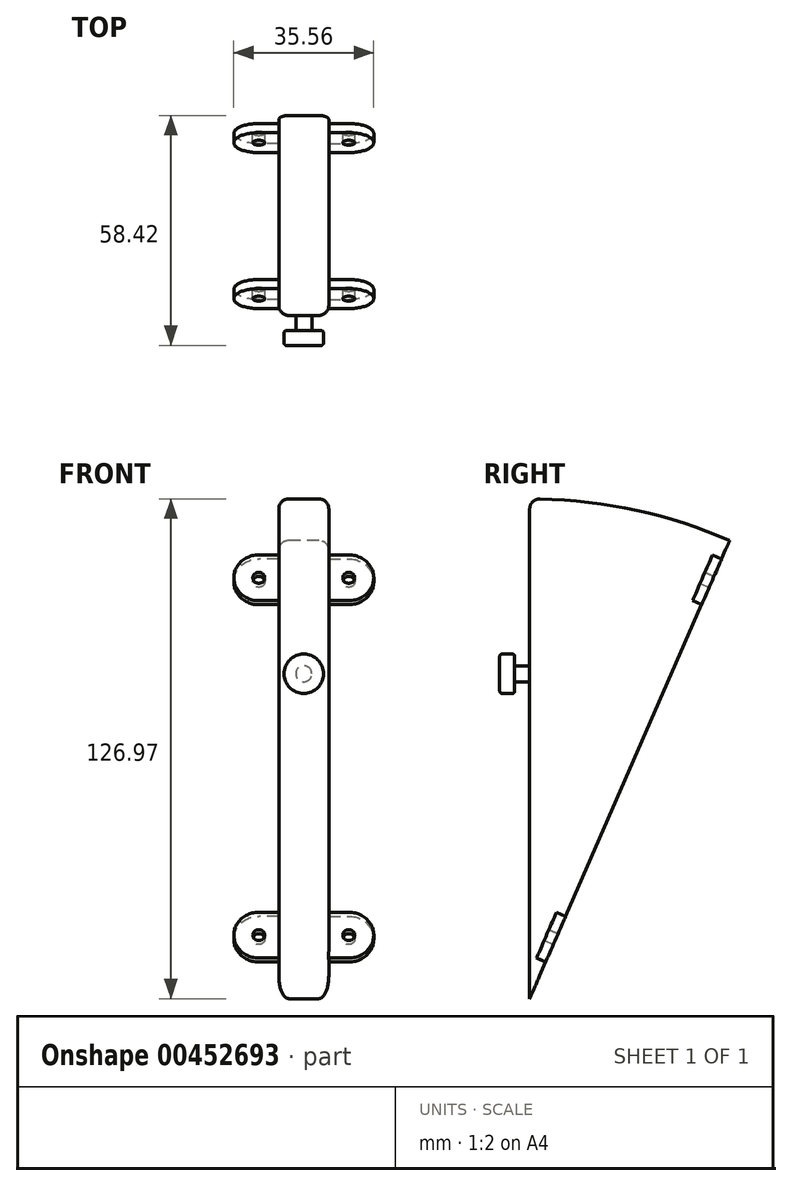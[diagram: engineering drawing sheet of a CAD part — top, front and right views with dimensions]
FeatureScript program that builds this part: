
annotation { "Feature Type Name" : "Feature", "Feature Type Description" : "" }
export const myFeature = defineFeature(function(context is Context, id is Id, definition is map)
    precondition{}
    {
        {
            var Q0;
            Q0=qCreatedBy(makeId("Front.planeOp"),FACE);
            var sketch = newSketch(context, id + "F0", { "sketchPlane" : qUnion([Q0])});
            skLineSegment(sketch, "E0", {"start": v(-25.33, 83.67) * mm, "end": v(-25.33, -43.33) * mm});
            skLineSegment(sketch, "E1", {"start": v(-25.33, -43.33) * mm, "end": v(-12.63, -43.33) * mm});
            skLineSegment(sketch, "E2", {"start": v(-12.63, -43.33) * mm, "end": v(-12.63, 83.67) * mm});
            skLineSegment(sketch, "E3", {"start": v(-12.63, 83.67) * mm, "end": v(-25.33, 83.67) * mm});
            skSolve(sketch);
        }
        {
            var Q0;
            Q0=makeQuery(id+"F0.imprint","IMPRINT",FACE,{"disambiguationData":[TD([[makeQuery(id+"F0.imprint","IMPRINT",EDGE,{"derivedFrom":sQuery(id+"F0.wireOp",EDGE,"E0")}),1.0]])]});
            var Q1;
            Q1=sQuery(id+"F0.wireOp",EDGE,"E1");
            revolve(context, id + "F1", {"entities" : qUnion([Q0]), "axis" : qUnion([Q1]), "revolveType" : RevolveType.ONE_DIRECTION, "oppositeDirection" : true, "angle" : 23.58 * degree});
        }
        {
            var Q0;
            Q0=makeQuery(id+"F1.opRevolve","CAP_FACE",FACE,{"disambiguationData":[OSD([sQuery(id+"F0.wireOp",EDGE,"E0"),sQuery(id+"F0.wireOp",EDGE,"E1"),sQuery(id+"F0.wireOp",EDGE,"E2"),sQuery(id+"F0.wireOp",EDGE,"E3")])],"isStart":false});
            var sketch = newSketch(context, id + "F2", { "sketchPlane" : qUnion([Q0])});
            skLineSegment(sketch, "E4", {"start": v(25.33, 87.28) * mm, "end": v(25.33, 82.2) * mm, "construction": true});
            skLineSegment(sketch, "E5", {"start": v(12.63, 87.28) * mm, "end": v(12.63, 82.2) * mm, "construction": true});
            skLineSegment(sketch, "E6", {"start": v(25.33, -39.72) * mm, "end": v(25.33, -29.56) * mm, "construction": true});
            skLineSegment(sketch, "E7", {"start": v(12.63, -39.72) * mm, "end": v(12.63, -29.56) * mm, "construction": true});
            skLineSegment(sketch, "E8", {"start": v(25.33, 82.2) * mm, "end": v(30.4, 82.2) * mm});
            skLineSegment(sketch, "E9", {"start": v(25.33, 82.2) * mm, "end": v(25.33, 69.5) * mm, "construction": true});
            skLineSegment(sketch, "E10", {"start": v(12.63, 82.2) * mm, "end": v(12.63, 69.5) * mm, "construction": true});
            skLineSegment(sketch, "E11", {"start": v(12.63, 82.2) * mm, "end": v(7.55, 82.2) * mm});
            skLineSegment(sketch, "E12", {"start": v(12.63, 69.5) * mm, "end": v(7.55, 69.5) * mm});
            skLineSegment(sketch, "E13", {"start": v(25.3, 69.5) * mm, "end": v(30.39, 69.5) * mm});
            skArc(sketch, "E14", {"start": v(30.4, 82.2) * mm, "mid": v(36.76, 75.84) * mm, "end": v(30.39, 69.5) * mm});
            skArc(sketch, "E15", {"start": v(7.55, 82.2) * mm, "mid": v(1.2, 75.85) * mm, "end": v(7.55, 69.5) * mm});
            skLineSegment(sketch, "E16", {"start": v(12.63, -29.56) * mm, "end": v(12.63, -16.86) * mm, "construction": true});
            skLineSegment(sketch, "E17", {"start": v(25.33, -29.56) * mm, "end": v(25.33, -16.86) * mm, "construction": true});
            skLineSegment(sketch, "E18", {"start": v(25.33, -16.86) * mm, "end": v(30.4, -16.86) * mm});
            skLineSegment(sketch, "E19", {"start": v(25.33, -29.56) * mm, "end": v(30.4, -29.56) * mm});
            skLineSegment(sketch, "E20", {"start": v(12.63, -29.56) * mm, "end": v(7.55, -29.56) * mm});
            skLineSegment(sketch, "E21", {"start": v(12.63, -16.86) * mm, "end": v(7.55, -16.86) * mm});
            skArc(sketch, "E22", {"start": v(7.55, -16.86) * mm, "mid": v(1.2, -23.2) * mm, "end": v(7.55, -29.56) * mm});
            skArc(sketch, "E23", {"start": v(30.4, -16.86) * mm, "mid": v(36.76, -23.2) * mm, "end": v(30.4, -29.56) * mm});
            skCircle(sketch, "E24", {"center": v(7.55, -23.2) * mm, "radius": 1.52 * mm});
            skCircle(sketch, "E25", {"center": v(30.4, -23.2) * mm, "radius": 1.52 * mm});
            skCircle(sketch, "E26", {"center": v(30.4, 75.85) * mm, "radius": 1.52 * mm});
            skCircle(sketch, "E27", {"center": v(7.55, 75.85) * mm, "radius": 1.52 * mm});
            skSolve(sketch);
        }
        {
            var Q0;
            {var subQ4=sQuery(id+"F2.wireOp",EDGE,"E8");Q0=makeQuery(id+"F2.imprint","IMPRINT",FACE,{"disambiguationData":[TD([[makeQuery(id+"F2.imprint","IMPRINT",EDGE,{"derivedFrom":subQ4}),-1.0]])]});}
            var Q1;
            {var subQ0=sQuery(id+"F2.wireOp",EDGE,"E11");Q1=makeQuery(id+"F2.imprint","IMPRINT",FACE,{"disambiguationData":[TD([[makeQuery(id+"F2.imprint","IMPRINT",EDGE,{"derivedFrom":subQ0}),1.0]])]});}
            var Q2;
            {var subQ1=sQuery(id+"F2.wireOp",EDGE,"E18");Q2=makeQuery(id+"F2.imprint","IMPRINT",FACE,{"disambiguationData":[TD([[makeQuery(id+"F2.imprint","IMPRINT",EDGE,{"derivedFrom":subQ1}),-1.0]])]});}
            var Q3;
            {var subQ1=sQuery(id+"F2.wireOp",EDGE,"E20");Q3=makeQuery(id+"F2.imprint","IMPRINT",FACE,{"disambiguationData":[TD([[makeQuery(id+"F2.imprint","IMPRINT",EDGE,{"derivedFrom":subQ1}),-1.0]])]});}
            extrude(context, id + "F3", {"entities" : qUnion([Q0, Q1, Q2, Q3]), "operationType" : NewBodyOperationType.ADD, "oppositeDirection" : true, "depth" : 2.54 * mm});
        }
        {
            var Q0;
            Q0=makeQuery(id+"F1.opRevolve","CAP_FACE",FACE,{"disambiguationData":[OSD([sQuery(id+"F0.wireOp",EDGE,"E0"),sQuery(id+"F0.wireOp",EDGE,"E1"),sQuery(id+"F0.wireOp",EDGE,"E2"),sQuery(id+"F0.wireOp",EDGE,"E3")])],"isStart":true});
            var sketch = newSketch(context, id + "F4", { "sketchPlane" : qUnion([Q0])});
            skCircle(sketch, "E28", {"center": v(-18.98, 39.22) * mm, "radius": 2.03 * mm});
            skSolve(sketch);
        }
        {
            var Q0;
            Q0=makeQuery(id+"F4.imprint","IMPRINT",FACE,{"disambiguationData":[TD([[makeQuery(id+"F4.imprint","IMPRINT",EDGE,{"derivedFrom":sQuery(id+"F4.wireOp",EDGE,"E28")}),1.0]])]});
            extrude(context, id + "F5", {"entities" : qUnion([Q0]), "operationType" : NewBodyOperationType.ADD, "depth" : 3.8 * mm});
        }
        {
            var Q0;
            Q0=makeQuery(id+"F5.opExtrude","CAP_FACE",FACE,{"disambiguationData":[OSD([sQuery(id+"F4.wireOp",EDGE,"E28")])],"isStart":false});
            var sketch = newSketch(context, id + "F6", { "sketchPlane" : qUnion([Q0])});
            skCircle(sketch, "E29.0", {"center": v(-18.98, 39.22) * mm, "radius": 2.03 * mm});
            skCircle(sketch, "E30", {"center": v(-18.98, 39.22) * mm, "radius": 5.02 * mm});
            skSolve(sketch);
        }
        {
            var Q0;
            Q0=makeQuery(id+"F6.imprint","IMPRINT",FACE,{"disambiguationData":[TD([[makeQuery(id+"F6.imprint","IMPRINT",EDGE,{"derivedFrom":sQuery(id+"F6.wireOp",EDGE,"E29.0")}),-1.0]])]});
            var Q1;
            Q1=makeQuery(id+"F6.imprint","IMPRINT",FACE,{"disambiguationData":[TD([[makeQuery(id+"F6.imprint","IMPRINT",EDGE,{"derivedFrom":sQuery(id+"F6.wireOp",EDGE,"E29.0")}),1.0]])]});
            extrude(context, id + "F7", {"entities" : qUnion([Q0, Q1]), "operationType" : NewBodyOperationType.ADD, "depth" : 3.8 * mm});
        }
        {
            var Q0;
            Q0=makeQuery(id+"F7.opExtrude","CAP_EDGE",EDGE,{"disambiguationData":[OSD([sQuery(id+"F6.wireOp",EDGE,"E30")])],"isStart":true});
            fillet(context, id + "F8", {"entities" : qUnion([Q0]), "radius" : 0.64 * mm, "tangentPropagation" : true, "allowEdgeOverflow" : false});
        }
        {
            var Q0;
            Q0=makeQuery(id+"F7.opExtrude","CAP_EDGE",EDGE,{"disambiguationData":[OSD([sQuery(id+"F6.wireOp",EDGE,"E30")])],"isStart":false});
            fillet(context, id + "F9", {"entities" : qUnion([Q0]), "radius" : 0.64 * mm, "tangentPropagation" : true, "allowEdgeOverflow" : false});
        }
        {
            var Q0;
            Q0=makeQuery(id+"F1.opRevolve","CAP_EDGE",EDGE,{"disambiguationData":[OSD([sQuery(id+"F0.wireOp",EDGE,"E0")])],"isStart":true});
            var Q1;
            Q1=makeQuery(id+"F1.opRevolve","CAP_EDGE",EDGE,{"disambiguationData":[OSD([sQuery(id+"F0.wireOp",EDGE,"E2")])],"isStart":true});
            var Q2;
            Q2=makeQuery(id+"F1.opRevolve","CAP_EDGE",EDGE,{"disambiguationData":[OSD([sQuery(id+"F0.wireOp",EDGE,"E3")])],"isStart":true});
            var Q3;
            Q3=makeQuery(id+"F1.opRevolve","SWEPT_EDGE",EDGE,{"disambiguationData":[OSD([sQuery(id+"F0.wireOp",EDGE,"E2"),sQuery(id+"F0.wireOp",EDGE,"E3")])]});
            var Q4;
            Q4=makeQuery(id+"F1.opRevolve","SWEPT_EDGE",EDGE,{"disambiguationData":[OSD([sQuery(id+"F0.wireOp",EDGE,"E0"),sQuery(id+"F0.wireOp",EDGE,"E3")])]});
            fillet(context, id + "F10", {"entities" : qUnion([Q0, Q1, Q2, Q3, Q4]), "radius" : 2.54 * mm, "tangentPropagation" : true, "allowEdgeOverflow" : false});
        }
    });
